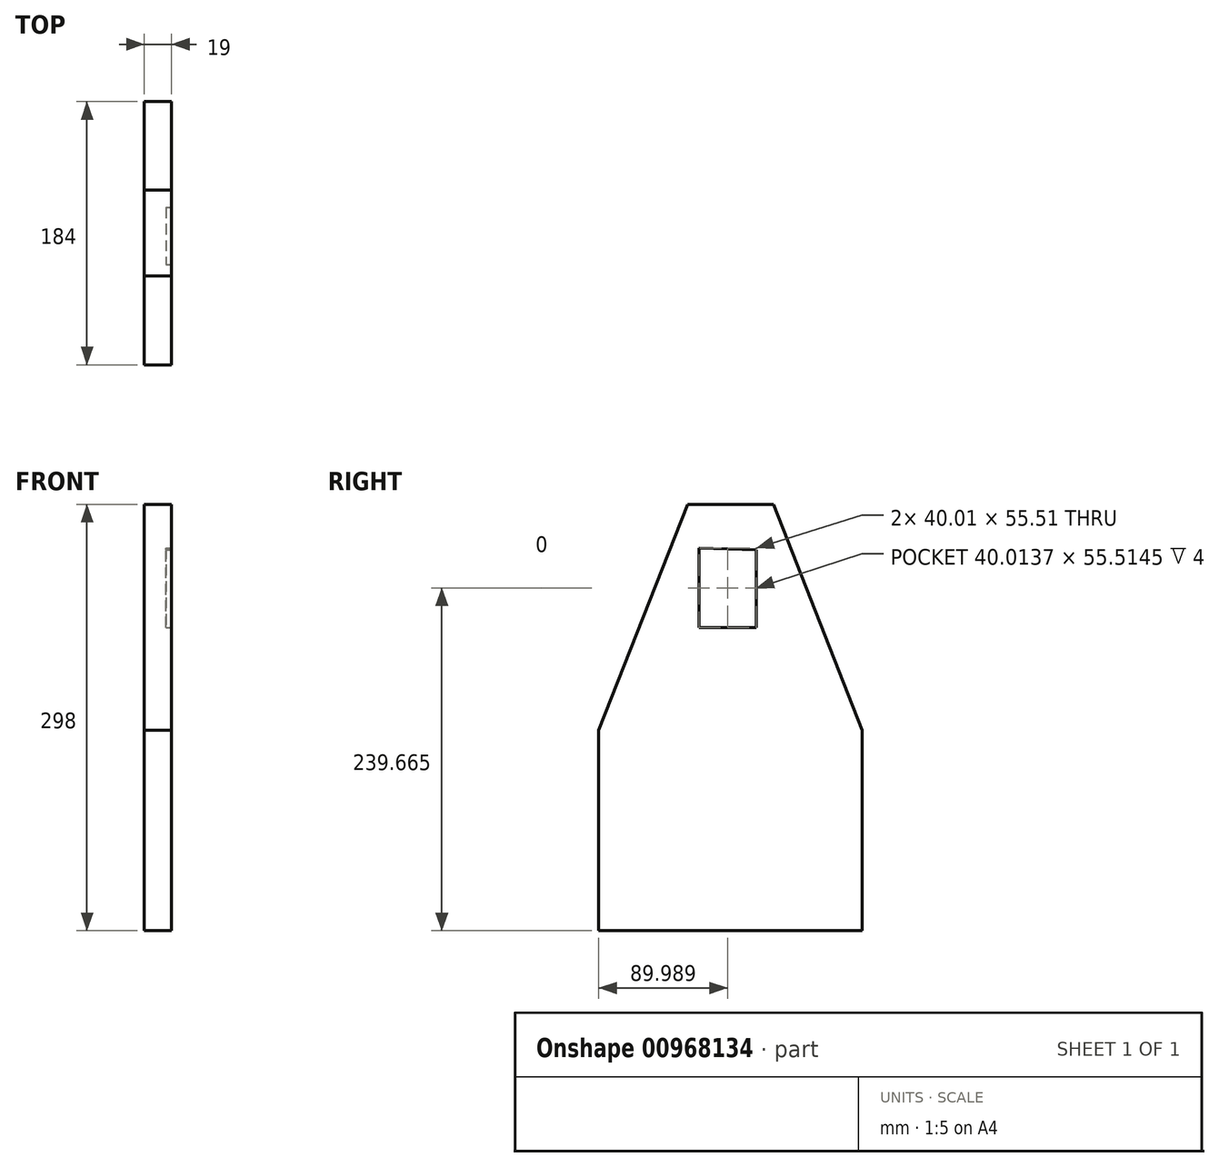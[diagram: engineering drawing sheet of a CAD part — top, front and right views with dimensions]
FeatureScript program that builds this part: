
annotation { "Feature Type Name" : "Feature", "Feature Type Description" : "" }
export const myFeature = defineFeature(function(context is Context, id is Id, definition is map)
    precondition{}
    {
        {
            var Q0;
            Q0=qCreatedBy(makeId("Right.planeOp"),FACE);
            var sketch = newSketch(context, id + "F0", { "sketchPlane" : qUnion([Q0])});
            skLineSegment(sketch, "E0.bottom", {"start": v(-53.07, 163.45) * mm, "end": v(6.93, 163.45) * mm});
            skLineSegment(sketch, "E0.left", {"start": v(-115.07, 5.45) * mm, "end": v(-115.07, -134.55) * mm});
            skLineSegment(sketch, "E0.right", {"start": v(68.93, 5.45) * mm, "end": v(68.93, -134.55) * mm});
            skLineSegment(sketch, "E1", {"start": v(-115.07, 5.45) * mm, "end": v(-53.07, 163.45) * mm});
            skLineSegment(sketch, "E2", {"start": v(6.93, 163.45) * mm, "end": v(68.93, 5.45) * mm});
            skLineSegment(sketch, "E3", {"start": v(-115.07, -134.55) * mm, "end": v(68.93, -134.55) * mm});
            skSolve(sketch);
        }
        {
            var Q0;
            Q0 = qSketchRegion(id + "F0", true);
            extrude(context, id + "F1", {"entities" : qUnion([Q0]), "depth" : 19 * mm, "offsetDistance" : 25 * mm});
        }
        {
            var Q0;
            Q0=makeQuery(id+"F1.opExtrude","CAP_FACE",FACE,{"disambiguationData":[OSD([sQuery(id+"F0.wireOp",EDGE,"E0.bottom"),sQuery(id+"F0.wireOp",EDGE,"E0.left"),sQuery(id+"F0.wireOp",EDGE,"E0.right"),sQuery(id+"F0.wireOp",EDGE,"E1"),sQuery(id+"F0.wireOp",EDGE,"E2"),sQuery(id+"F0.wireOp",EDGE,"E3")])],"isStart":false});
            var sketch = newSketch(context, id + "F2", { "sketchPlane" : qUnion([Q0])});
            skLineSegment(sketch, "E4", {"start": v(-45.09, 132.87) * mm, "end": v(-45.09, 77.36) * mm});
            skLineSegment(sketch, "E5", {"start": v(-5.07, 77.36) * mm, "end": v(-45.09, 77.36) * mm});
            skLineSegment(sketch, "E6", {"start": v(-5.07, 77.36) * mm, "end": v(-5.07, 131.8) * mm});
            skLineSegment(sketch, "E7", {"start": v(-5.07, 131.8) * mm, "end": v(-45.09, 132.87) * mm});
            skLineSegment(sketch, "E8", {"start": v(-31.04, 132.5) * mm, "end": v(-25.08, 132.33) * mm, "construction": true});
            skSolve(sketch);
        }
        {
            var Q0;
            Q0 = qSketchRegion(id + "F2", true);
            extrude(context, id + "F3", {"entities" : qUnion([Q0]), "operationType" : NewBodyOperationType.REMOVE, "oppositeDirection" : true, "depth" : 4 * mm, "offsetDistance" : 25 * mm});
        }
    });
